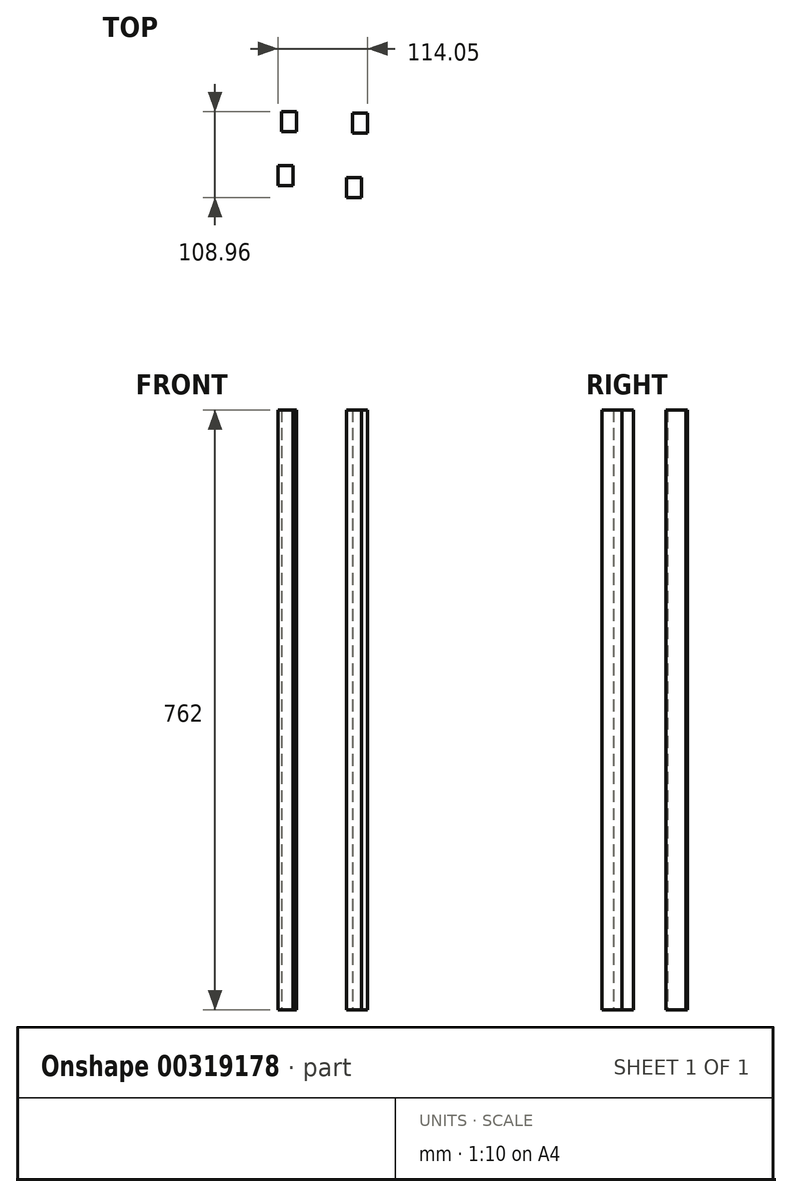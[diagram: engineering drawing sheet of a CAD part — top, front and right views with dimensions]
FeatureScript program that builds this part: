
annotation { "Feature Type Name" : "Feature", "Feature Type Description" : "" }
export const myFeature = defineFeature(function(context is Context, id is Id, definition is map)
    precondition{}
    {
        {
            var Q0;
            Q0=qCreatedBy(makeId("Top.planeOp"),FACE);
            var sketch = newSketch(context, id + "F0", { "sketchPlane" : qUnion([Q0])});
            skLineSegment(sketch, "E0.bottom", {"start": v(-62.23, -5.45) * mm, "end": v(-43.18, -5.45) * mm});
            skLineSegment(sketch, "E0.top", {"start": v(-62.23, -30.85) * mm, "end": v(-43.18, -30.85) * mm});
            skLineSegment(sketch, "E0.left", {"start": v(-62.23, -5.45) * mm, "end": v(-62.23, -30.85) * mm});
            skLineSegment(sketch, "E0.right", {"start": v(-43.18, -5.45) * mm, "end": v(-43.18, -30.85) * mm});
            skSolve(sketch);
        }
        {
            var Q0;
            Q0=makeQuery(id+"F0.imprint","IMPRINT",FACE,{"disambiguationData":[TD([[makeQuery(id+"F0.imprint","IMPRINT",EDGE,{"derivedFrom":sQuery(id+"F0.wireOp",EDGE,"E0.bottom")}),-1.0]])]});
            extrude(context, id + "F1", {"entities" : qUnion([Q0]), "depth" : 762 * mm});
        }
        {
            var Q0;
            Q0=qCreatedBy(makeId("Top.planeOp"),FACE);
            var sketch = newSketch(context, id + "F2", { "sketchPlane" : qUnion([Q0])});
            skLineSegment(sketch, "E1.bottom", {"start": v(-57.91, 63.24) * mm, "end": v(-38.86, 63.24) * mm});
            skLineSegment(sketch, "E1.top", {"start": v(-57.91, 37.84) * mm, "end": v(-38.86, 37.84) * mm});
            skLineSegment(sketch, "E1.left", {"start": v(-57.91, 63.24) * mm, "end": v(-57.91, 37.84) * mm});
            skLineSegment(sketch, "E1.right", {"start": v(-38.86, 63.24) * mm, "end": v(-38.86, 37.84) * mm});
            skLineSegment(sketch, "E2.bottom", {"start": v(32.77, 61.21) * mm, "end": v(51.82, 61.21) * mm});
            skLineSegment(sketch, "E2.top", {"start": v(32.77, 35.81) * mm, "end": v(51.82, 35.81) * mm});
            skLineSegment(sketch, "E2.left", {"start": v(32.77, 61.21) * mm, "end": v(32.77, 35.81) * mm});
            skLineSegment(sketch, "E2.right", {"start": v(51.82, 61.21) * mm, "end": v(51.82, 35.81) * mm});
            skLineSegment(sketch, "E3.bottom", {"start": v(24.64, -20.32) * mm, "end": v(43.69, -20.32) * mm});
            skLineSegment(sketch, "E3.top", {"start": v(24.64, -45.72) * mm, "end": v(43.69, -45.72) * mm});
            skLineSegment(sketch, "E3.left", {"start": v(24.64, -20.32) * mm, "end": v(24.64, -45.72) * mm});
            skLineSegment(sketch, "E3.right", {"start": v(43.69, -20.32) * mm, "end": v(43.69, -45.72) * mm});
            skSolve(sketch);
        }
        {
            var Q0;
            Q0=makeQuery(id+"F2.imprint","IMPRINT",FACE,{"disambiguationData":[TD([[makeQuery(id+"F2.imprint","IMPRINT",EDGE,{"derivedFrom":sQuery(id+"F2.wireOp",EDGE,"E1.bottom")}),-1.0]])]});
            var Q1;
            Q1=makeQuery(id+"F2.imprint","IMPRINT",FACE,{"disambiguationData":[TD([[makeQuery(id+"F2.imprint","IMPRINT",EDGE,{"derivedFrom":sQuery(id+"F2.wireOp",EDGE,"E2.bottom")}),-1.0]])]});
            var Q2;
            Q2=makeQuery(id+"F2.imprint","IMPRINT",FACE,{"disambiguationData":[TD([[makeQuery(id+"F2.imprint","IMPRINT",EDGE,{"derivedFrom":sQuery(id+"F2.wireOp",EDGE,"E3.bottom")}),-1.0]])]});
            extrude(context, id + "F3", {"entities" : qUnion([Q0, Q1, Q2]), "depth" : 762 * mm});
        }
    });
